# Revit family: ToothbrushHolder-Vitra-İstanbulSeries-A48017
name_source: partatom
category: Plumbing Fixtures
revit_build: Autodesk Revit 2017 (Build: 20160225_1515(x64)
units: mm (PartAtom-declared; Revit-internal decimal feet)

## family parameters
Cut with Voids When Loaded = No
Host = Face
OmniClass Number = 23.45.00.00
OmniClass Title = Sanitary, Laundry, and Cleaning Equipment
Part Type = Normal
Room Calculation Point = No
Round Connector Dimension = Use Diameter
Shared = Yes

## types (11) — shared parameters
BIMobject category = Sanitary - Accessories
Brand = VitrA
CW Connection = No
Default Elevation = 1200 mm
Description = İstanbul Toothbrush Holder
Design country = Turkey
HW Connection = No
IFC Classification = Sanitary Terminal
Manufacturer = Vitra
Manufacturer name = Vitra
Masterformat 2014 Code = 10 28 16
Masterformat 2014 Description = Bath Accessories
Mounting type = Wall Mounted
NBS Referans Code = 35-75-89
NBS Referans Description = Toothbrush Holders
Nominal Depth (mm) = 90 mm
Nominal Height (mm) = 85 mm  [stored 0.278871 ft]
Nominal Width (mm) = 135 mm  [stored 0.442913 ft]
OmniClass Code = 23-31 25 00
OmniClass Description = Toilet and Bath Specialties
Primary Material = White
Product Type = Built-in Toothbrush Holder
Product certification = https://www.vitraglobal.com
Product family = İstanbulSeries
Product group = Toothbrush Holder
UNSPSC Description = Furniture and Furnishings
URL = https://vitraglobal.com
Uniclass 1.4 Code = L824
Uniclass 1.4 Description = Bathroom, toilet furniture and fittings
Uniclass 2.0 Code = PR-35-75-89
Uniclass 2.0 Description = Toothbrush Holders
Uniclass 2015 Code = Pr_40_20_76_89
Uniclass 2015 Name = Toothbrush holders
Uniformat II Code = E20
Uniformat II Description = FURNISHINGS
Vent Connection = No
Warranty Period (Year) = 5 Years
Waste Connection = No
Weight Net (kg) = 1.035
Youtube = https://www.youtube.com

## per-type parameters (varying)
| type | Article No. (default) | Coating Material | Color | Model | Product SKU | Product data url | Technical description |
| ToothBrushHolder-Vitra-İstanbulSeries(White)-A4801799EXP | A4801799EXP | White | White | A4801799EXP | A4801799EXP | https://www.vitraglobal.com | https://www.vitraglobal.com |
| ToothBrushHolder-Vitra-İstanbulSeries(White)-A4801799 | A4801799 | White | White | A4801799 | A4801799 | https://www.vitraglobal.com | https://www.vitraglobal.com |
| ToothBrushHolder-Vitra-İstanbulSeries(Black)-A4801792EXP | A4801792EXP | Black | Black | A4801792EXP | A4801792EXP | https://www.vitraglobal.com | https://www.vitraglobal.com |
| ToothBrushHolder-Vitra-İstanbulSeries(Black)-A4801792 | A4801792 | Black | Black | A4801792 | A4801792 | https://www.vitraglobal.com | https://www.vitraglobal.com |
| ToothBrushHolder-Vitra-İstanbulSeries(Chrome)-A48017VUK | A48017VUK | Chrome | Chrome | A48017VUK | A48017VUK | https://www.vitra.co.uk | https://www.vitra.co.uk |
| ToothBrushHolder-Vitra-İstanbulSeries(Chrome)-A48017IND | A48017IND | Chrome | Chrome | A48017IND | A48017IND | https://www.vitraglobal.com | https://www.vitraglobal.com |
| ToothBrushHolder-Vitra-İstanbulSeries(Chrome)-A48017EXP | A48017EXP | Chrome | Chrome | A48017EXP | A48017EXP | https://www.vitraglobal.com | https://www.vitraglobal.com |
| ToothBrushHolder-Vitra-İstanbulSeries(Gold)-A4801723VUK | A4801723VUK | Gold | Gold | A4801723VUK | A4801723VUK | https://www.vitra.co.uk | https://www.vitra.co.uk |
| ToothBrushHolder-Vitra-İstanbulSeries(Gold)-A4801723EXP | A4801723EXP | Gold | Gold | A4801723EXP | A4801723EXP | https://www.vitraglobal.com | https://www.vitraglobal.com |
| ToothBrushHolder-Vitra-İstanbulSeries(Gold)-A4801723 | A4801723 | Gold | Gold | A4801723 | A4801723 | https://www.vitraglobal.com | https://www.vitraglobal.com |
| ToothBrushHolder-Vitra-İstanbulSeries(Chrome)-A48017 | A48017 | Chrome | Chrome | A48017 | A48017 | https://www.vitraglobal.com | https://www.vitraglobal.com |

note: [stored X ft] marks values corroborated as IEEE doubles in the binary element streams (Revit-internal decimal feet)

## geometry (parser evidence)
native form markers: Sweep x2
no freeform markers — native parametric forms only
